# Revit family: Grohe_PlumbingFixture_Tempesta-FTriggerSpray30_WallHolderSet1Spray_27513001a
name_source: partatom
category: Plumbing Fixtures
revit_build: Autodesk Revit 2018 (Build: 20190510_1515(x64)
units: mm (PartAtom-declared; Revit-internal decimal feet)

## family parameters
Cut with Voids When Loaded = No
Host = Face
OmniClass Number = 23.65.00.00
OmniClass Title = Supply and Distribution of Liquids and Gases
Part Type = Normal
Room Calculation Point = No
Round Connector Dimension = Use Diameter
Shared = No

## types (1)
- 27513001
    ADACompliant = No
    Assembly Code = D2010
    AssetType = Fixed
    BIMObjectName = Grohe_PlumbingFixture_Tempesta-FTriggerSpray30_WallHolderSet1Spray_27513001
    CWFU = 0
    ClassificationName = Uniclass 2015
    ClassificationValue = Pr_40_20_87_76
    ColdWaterConnectionDiameter = 10 mm  [stored 0.0328084 ft]
    Color = Chrome
    Cost = 0 $
    Default Elevation = 0 mm  [stored 0 ft]
    Description = Add ultimate functionality to your perfect home bathroom by fitting a New Tempesta-F Trigger Spray 30 wall holder set. The spray offers accurate, powerful cleaning for extra convenience and hygiene, with the trigger giving precise control and the TwistFree hose ensuring you don’t get in a tangle. The head’s spray plate is detachable for easy cleaning and its SpeedClean nozzles are designed to brush free of limescale with a simple wipe. A durable but dazzling GROHE StarLight chrome finish keeps it looking stunning. A super-insulated Inner WaterGuide prevents the surface from getting too hot, protecting both your skin, and the lustrous chrome finish. Built with German engineering you can trust, add this useful, affordable extra detail to your bathroom today. Please refer to local regulations regarding installation.
    DocumentationCertificates = www.grohe.co.uk/
    DocumentationInstallationGuide = www.grohe.co.uk/
    DocumentationLiterature = www.grohe.co.uk/
    DocumentationMaintenance = www.grohe.co.uk/
    DocumentationTechnical = www.grohe.co.uk/
    DurationUnit = Years
    Ecojoy = No
    ExpectedLife = 0
    FaucetMaterial = Grohe-Chrome
    Features = Consisting of: 
hand shower with trigger control (27 512 001) 
wall shower holder (28 605) 
Silverflex Longlife shower hose 1250 mm (26 335) 
GROHE StarLight chrome finish 
SpeedClean anti-limescale system 
Inner WaterGuide for a longer life 
Twistfree preventing the hose from twisting 
Please refer to local norms regarding installation.
    HWFU = 0
    HotWaterConnectionDiameter = 10 mm  [stored 0.0328084 ft]
    IfcExportAs = IfcPipeFitting
    IfcExportType = IfcPipeFittingType
    Keynote = N13
    LowEmittingMaterial = No
    Manufacturer = Grohe
    ManufacturerName = Grohe
    MasterformatNumber = 01 52 19
    MasterformatTitle = Sanitary Facilities
    Model = TEMPESTA-F TRIGGER SPRAY 30
    ModelNumber = 27513001
    ModelReference = TEMPESTA-F TRIGGER SPRAY 30 - WALL HOLDER SET 1 SPRAY
    NBSDescription = Shower heads
    NBSObjectName = Grohe - Shower heads
    NBSReference = 45-35-70/333
    NominalDepth = 0 mm  [stored 0 ft]
    NominalHeight = 0 mm  [stored 0 ft]
    NominalLength = 0 mm  [stored 0 ft]
    ProductPageURL = https://www.grohe.co.uk
    ProductionYear = 2020
    Type Comments = WALL HOLDER SET 1 SPRAY
    TypeName = TEMPESTA-F TRIGGER SPRAY 30 - WALL HOLDER SET 1 SPRAY
    URL = www.grohe.com
    WarrantyDurationLabor = 0
    WarrantyDurationParts = 0
    WarrantyDurationUnit = Years
    _BSBibleVersion = 16
    _BimSpecGuid = 0
    _CurrentRevision = 1
    _DistributedBy = www.bimstore.co
    _ObjectUserGuide = www.bimstore.co

note: [stored X ft] marks values corroborated as IEEE doubles in the binary element streams (Revit-internal decimal feet)

## geometry (parser evidence)
native form markers: Sweep x2
no freeform markers — native parametric forms only
